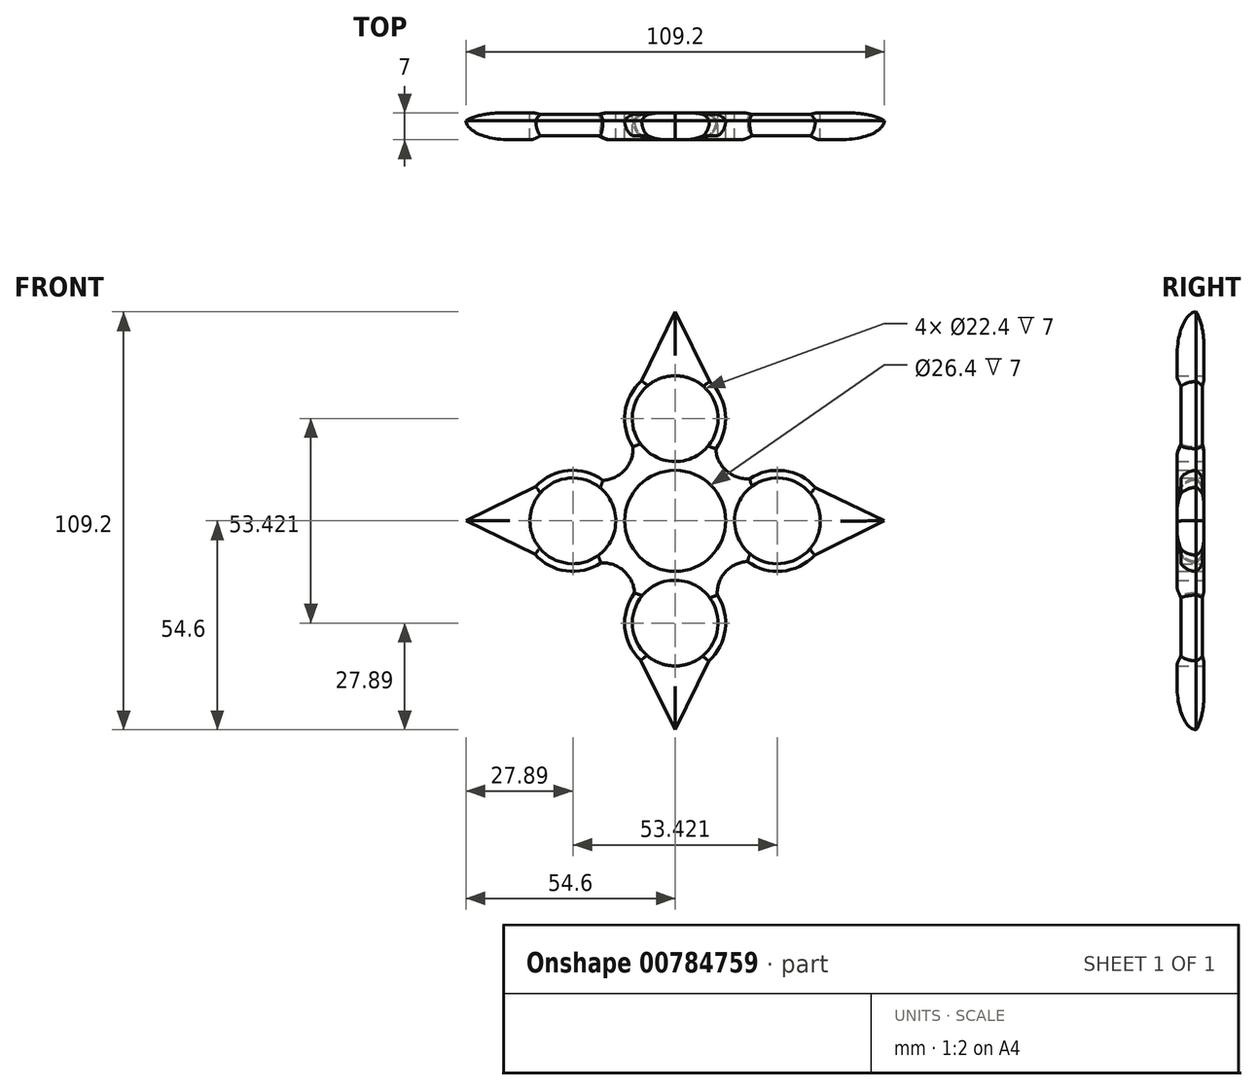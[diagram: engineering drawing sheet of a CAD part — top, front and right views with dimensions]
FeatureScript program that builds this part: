
annotation { "Feature Type Name" : "Feature", "Feature Type Description" : "" }
export const myFeature = defineFeature(function(context is Context, id is Id, definition is map)
    precondition{}
    {
        {
            var Q0;
            Q0=qCreatedBy(makeId("Front.planeOp"),FACE);
            var sketch = newSketch(context, id + "F0", { "sketchPlane" : qUnion([Q0])});
            skCircle(sketch, "E0", {"center": v(0, 0) * mm, "radius": 11.2 * mm});
            skCircle(sketch, "E1", {"center": v(0, 0) * mm, "radius": 13.2 * mm});
            skCircle(sketch, "E2", {"center": v(0, 26.71) * mm, "radius": 11.2 * mm});
            skArc(sketch, "E3", {"start": v(10.62, 18.87) * mm, "mid": v(0.33, 39.9) * mm, "end": v(-11, 19.4) * mm});
            skArc(sketch, "E4.1.0", {"start": v(-18.87, 10.62) * mm, "mid": v(-39.9, 0.33) * mm, "end": v(-19.4, -11) * mm});
            skCircle(sketch, "E4.1.1", {"center": v(-26.71, 0) * mm, "radius": 11.2 * mm});
            skArc(sketch, "E4.2.0", {"start": v(-10.62, -18.87) * mm, "mid": v(-0.33, -39.9) * mm, "end": v(11, -19.4) * mm});
            skCircle(sketch, "E4.2.1", {"center": v(0, -26.71) * mm, "radius": 11.2 * mm});
            skArc(sketch, "E5.1.3.0", {"start": v(18.87, -10.62) * mm, "mid": v(39.9, -0.33) * mm, "end": v(19.4, 11) * mm});
            skCircle(sketch, "E5.2.3.0", {"center": v(26.71, 0) * mm, "radius": 11.2 * mm});
            skArc(sketch, "E6", {"start": v(-18.87, 10.62) * mm, "mid": v(-13.1, 13.37) * mm, "end": v(-11, 19.4) * mm});
            skArc(sketch, "E7.1.0", {"start": v(-10.62, -18.87) * mm, "mid": v(-13.37, -13.1) * mm, "end": v(-19.4, -11) * mm});
            skArc(sketch, "E7.2.0", {"start": v(18.87, -10.62) * mm, "mid": v(13.1, -13.37) * mm, "end": v(11, -19.4) * mm});
            skArc(sketch, "E7.3.0", {"start": v(10.62, 18.87) * mm, "mid": v(13.37, 13.1) * mm, "end": v(19.4, 11) * mm});
            skLineSegment(sketch, "E8", {"start": v(-8.75, 36.6) * mm, "end": v(0, 54.6) * mm});
            skLineSegment(sketch, "E9", {"start": v(0, 54.6) * mm, "end": v(8.96, 36.4) * mm});
            skLineSegment(sketch, "E10.1.0", {"start": v(-54.6, 0) * mm, "end": v(-36.4, 8.96) * mm});
            skLineSegment(sketch, "E10.1.1", {"start": v(-36.6, -8.75) * mm, "end": v(-54.6, 0) * mm});
            skLineSegment(sketch, "E10.2.0", {"start": v(0, -54.6) * mm, "end": v(-8.96, -36.4) * mm});
            skLineSegment(sketch, "E10.2.1", {"start": v(8.75, -36.6) * mm, "end": v(0, -54.6) * mm});
            skLineSegment(sketch, "E10.3.0", {"start": v(54.6, 0) * mm, "end": v(36.4, -8.96) * mm});
            skLineSegment(sketch, "E10.3.1", {"start": v(36.6, 8.75) * mm, "end": v(54.6, 0) * mm});
            skSolve(sketch);
        }
        {
            var Q0;
            Q0=makeQuery(id+"F0.imprint","IMPRINT",FACE,{"disambiguationData":[TD([[makeQuery(id+"F0.imprint","IMPRINT",EDGE,{"derivedFrom":sQuery(id+"F0.wireOp",EDGE,"E1")}),-1.0]])]});
            var Q1;
            {var subQ0=sQuery(id+"F0.wireOp",EDGE,"E8");Q1=makeQuery(id+"F0.imprint","IMPRINT",FACE,{"disambiguationData":[TD([[makeQuery(id+"F0.imprint","IMPRINT",EDGE,{"derivedFrom":subQ0}),-1.0]])]});}
            var Q2;
            {var subQ0=sQuery(id+"F0.wireOp",EDGE,"E10.1.0");Q2=makeQuery(id+"F0.imprint","IMPRINT",FACE,{"disambiguationData":[TD([[makeQuery(id+"F0.imprint","IMPRINT",EDGE,{"derivedFrom":subQ0}),-1.0]])]});}
            var Q3;
            {var subQ0=sQuery(id+"F0.wireOp",EDGE,"E10.3.0");Q3=makeQuery(id+"F0.imprint","IMPRINT",FACE,{"disambiguationData":[TD([[makeQuery(id+"F0.imprint","IMPRINT",EDGE,{"derivedFrom":subQ0}),-1.0]])]});}
            var Q4;
            {var subQ0=sQuery(id+"F0.wireOp",EDGE,"E10.2.0");Q4=makeQuery(id+"F0.imprint","IMPRINT",FACE,{"disambiguationData":[TD([[makeQuery(id+"F0.imprint","IMPRINT",EDGE,{"derivedFrom":subQ0}),-1.0]])]});}
            extrude(context, id + "F1", {"entities" : qUnion([Q0, Q1, Q2, Q3, Q4]), "depth" : 7 * mm, "offsetDistance" : 25 * mm});
        }
        {
            var Q0;
            {var subQ0=sQuery(id+"F0.wireOp",EDGE,"E3");Q0=makeQuery(id+"F1.opExtrude","CAP_EDGE",EDGE,{"disambiguationData":[OSD([subQ0]),TDD([makeQuery(id+"F0.imprint","IMPRINT",EDGE,{"disambiguationData":[TD([[makeQuery(id+"F0.imprint","INTERSECT",VERTEX,{"derivedFrom":[subQ0,sQuery(id+"F0.wireOp",EDGE,"E6")]}),1.0]])],"derivedFrom":subQ0})])],"isStart":false});}
            var Q1;
            Q1=makeQuery(id+"F1.opExtrude","CAP_EDGE",EDGE,{"disambiguationData":[OSD([sQuery(id+"F0.wireOp",EDGE,"E8")])],"isStart":false});
            var Q2;
            Q2=makeQuery(id+"F1.opExtrude","CAP_EDGE",EDGE,{"disambiguationData":[OSD([sQuery(id+"F0.wireOp",EDGE,"E9")])],"isStart":false});
            var Q3;
            {var subQ0=sQuery(id+"F0.wireOp",EDGE,"E3");Q3=makeQuery(id+"F1.opExtrude","CAP_EDGE",EDGE,{"disambiguationData":[OSD([subQ0]),TDD([makeQuery(id+"F0.imprint","IMPRINT",EDGE,{"disambiguationData":[TD([[makeQuery(id+"F0.imprint","INTERSECT",VERTEX,{"derivedFrom":[subQ0,sQuery(id+"F0.wireOp",EDGE,"E7.3.0")]}),-1.0]])],"derivedFrom":subQ0})])],"isStart":false});}
            var Q4;
            Q4=makeQuery(id+"F1.opExtrude","CAP_EDGE",EDGE,{"disambiguationData":[OSD([sQuery(id+"F0.wireOp",EDGE,"E7.3.0")])],"isStart":false});
            var Q5;
            {var subQ0=sQuery(id+"F0.wireOp",EDGE,"E5.1.3.0");Q5=makeQuery(id+"F1.opExtrude","CAP_EDGE",EDGE,{"disambiguationData":[OSD([subQ0]),TDD([makeQuery(id+"F0.imprint","IMPRINT",EDGE,{"disambiguationData":[TD([[makeQuery(id+"F0.imprint","INTERSECT",VERTEX,{"derivedFrom":[subQ0,sQuery(id+"F0.wireOp",EDGE,"E7.3.0")]}),1.0]])],"derivedFrom":subQ0})])],"isStart":false});}
            var Q6;
            Q6=makeQuery(id+"F1.opExtrude","CAP_EDGE",EDGE,{"disambiguationData":[OSD([sQuery(id+"F0.wireOp",EDGE,"E10.3.1")])],"isStart":false});
            var Q7;
            Q7=makeQuery(id+"F1.opExtrude","CAP_EDGE",EDGE,{"disambiguationData":[OSD([sQuery(id+"F0.wireOp",EDGE,"E10.3.0")])],"isStart":false});
            var Q8;
            {var subQ0=sQuery(id+"F0.wireOp",EDGE,"E5.1.3.0");Q8=makeQuery(id+"F1.opExtrude","CAP_EDGE",EDGE,{"disambiguationData":[OSD([subQ0]),TDD([makeQuery(id+"F0.imprint","IMPRINT",EDGE,{"disambiguationData":[TD([[makeQuery(id+"F0.imprint","INTERSECT",VERTEX,{"derivedFrom":[subQ0,sQuery(id+"F0.wireOp",EDGE,"E7.2.0")]}),-1.0]])],"derivedFrom":subQ0})])],"isStart":false});}
            var Q9;
            Q9=makeQuery(id+"F1.opExtrude","CAP_EDGE",EDGE,{"disambiguationData":[OSD([sQuery(id+"F0.wireOp",EDGE,"E7.2.0")])],"isStart":false});
            var Q10;
            {var subQ0=sQuery(id+"F0.wireOp",EDGE,"E4.2.0");Q10=makeQuery(id+"F1.opExtrude","CAP_EDGE",EDGE,{"disambiguationData":[OSD([subQ0]),TDD([makeQuery(id+"F0.imprint","IMPRINT",EDGE,{"disambiguationData":[TD([[makeQuery(id+"F0.imprint","INTERSECT",VERTEX,{"derivedFrom":[subQ0,sQuery(id+"F0.wireOp",EDGE,"E7.2.0")]}),1.0]])],"derivedFrom":subQ0})])],"isStart":false});}
            var Q11;
            Q11=makeQuery(id+"F1.opExtrude","CAP_EDGE",EDGE,{"disambiguationData":[OSD([sQuery(id+"F0.wireOp",EDGE,"E10.2.1")])],"isStart":false});
            var Q12;
            Q12=makeQuery(id+"F1.opExtrude","CAP_EDGE",EDGE,{"disambiguationData":[OSD([sQuery(id+"F0.wireOp",EDGE,"E10.2.0")])],"isStart":false});
            var Q13;
            {var subQ0=sQuery(id+"F0.wireOp",EDGE,"E4.2.0");Q13=makeQuery(id+"F1.opExtrude","CAP_EDGE",EDGE,{"disambiguationData":[OSD([subQ0]),TDD([makeQuery(id+"F0.imprint","IMPRINT",EDGE,{"disambiguationData":[TD([[makeQuery(id+"F0.imprint","INTERSECT",VERTEX,{"derivedFrom":[subQ0,sQuery(id+"F0.wireOp",EDGE,"E7.1.0")]}),-1.0]])],"derivedFrom":subQ0})])],"isStart":false});}
            var Q14;
            Q14=makeQuery(id+"F1.opExtrude","CAP_EDGE",EDGE,{"disambiguationData":[OSD([sQuery(id+"F0.wireOp",EDGE,"E7.1.0")])],"isStart":false});
            var Q15;
            {var subQ0=sQuery(id+"F0.wireOp",EDGE,"E4.1.0");Q15=makeQuery(id+"F1.opExtrude","CAP_EDGE",EDGE,{"disambiguationData":[OSD([subQ0]),TDD([makeQuery(id+"F0.imprint","IMPRINT",EDGE,{"disambiguationData":[TD([[makeQuery(id+"F0.imprint","INTERSECT",VERTEX,{"derivedFrom":[subQ0,sQuery(id+"F0.wireOp",EDGE,"E7.1.0")]}),1.0]])],"derivedFrom":subQ0})])],"isStart":false});}
            var Q16;
            Q16=makeQuery(id+"F1.opExtrude","CAP_EDGE",EDGE,{"disambiguationData":[OSD([sQuery(id+"F0.wireOp",EDGE,"E10.1.1")])],"isStart":false});
            var Q17;
            Q17=makeQuery(id+"F1.opExtrude","CAP_EDGE",EDGE,{"disambiguationData":[OSD([sQuery(id+"F0.wireOp",EDGE,"E10.1.0")])],"isStart":false});
            var Q18;
            {var subQ0=sQuery(id+"F0.wireOp",EDGE,"E4.1.0");Q18=makeQuery(id+"F1.opExtrude","CAP_EDGE",EDGE,{"disambiguationData":[OSD([subQ0]),TDD([makeQuery(id+"F0.imprint","IMPRINT",EDGE,{"disambiguationData":[TD([[makeQuery(id+"F0.imprint","INTERSECT",VERTEX,{"derivedFrom":[subQ0,sQuery(id+"F0.wireOp",EDGE,"E6")]}),-1.0]])],"derivedFrom":subQ0})])],"isStart":false});}
            var Q19;
            Q19=makeQuery(id+"F1.opExtrude","CAP_EDGE",EDGE,{"disambiguationData":[OSD([sQuery(id+"F0.wireOp",EDGE,"E6")])],"isStart":false});
            fillet(context, id + "F2", {"entities" : qUnion([Q0, Q1, Q2, Q3, Q4, Q5, Q6, Q7, Q8, Q9, Q10, Q11, Q12, Q13, Q14, Q15, Q16, Q17, Q18, Q19]), "radius" : 5 * mm, "tangentPropagation" : true, "allowEdgeOverflow" : false});
        }
        {
            var Q0;
            Q0=makeQuery(id+"F1.opExtrude","CAP_EDGE",EDGE,{"disambiguationData":[OSD([sQuery(id+"F0.wireOp",EDGE,"E9")])],"isStart":true});
            var Q1;
            Q1=makeQuery(id+"F1.opExtrude","CAP_EDGE",EDGE,{"disambiguationData":[OSD([sQuery(id+"F0.wireOp",EDGE,"E8")])],"isStart":true});
            var Q2;
            Q2=makeQuery(id+"F1.opExtrude","CAP_EDGE",EDGE,{"disambiguationData":[OSD([sQuery(id+"F0.wireOp",EDGE,"E7.3.0")])],"isStart":true});
            var Q3;
            Q3=makeQuery(id+"F1.opExtrude","CAP_EDGE",EDGE,{"disambiguationData":[OSD([sQuery(id+"F0.wireOp",EDGE,"E6")])],"isStart":true});
            var Q4;
            Q4=makeQuery(id+"F1.opExtrude","CAP_EDGE",EDGE,{"disambiguationData":[OSD([sQuery(id+"F0.wireOp",EDGE,"E7.2.0")])],"isStart":true});
            var Q5;
            Q5=makeQuery(id+"F1.opExtrude","CAP_EDGE",EDGE,{"disambiguationData":[OSD([sQuery(id+"F0.wireOp",EDGE,"E7.1.0")])],"isStart":true});
            var Q6;
            Q6=makeQuery(id+"F1.opExtrude","CAP_EDGE",EDGE,{"disambiguationData":[OSD([sQuery(id+"F0.wireOp",EDGE,"E10.3.1")])],"isStart":true});
            var Q7;
            Q7=makeQuery(id+"F1.opExtrude","CAP_EDGE",EDGE,{"disambiguationData":[OSD([sQuery(id+"F0.wireOp",EDGE,"E10.3.0")])],"isStart":true});
            var Q8;
            Q8=makeQuery(id+"F1.opExtrude","CAP_EDGE",EDGE,{"disambiguationData":[OSD([sQuery(id+"F0.wireOp",EDGE,"E10.1.1")])],"isStart":true});
            var Q9;
            Q9=makeQuery(id+"F1.opExtrude","CAP_EDGE",EDGE,{"disambiguationData":[OSD([sQuery(id+"F0.wireOp",EDGE,"E10.1.0")])],"isStart":true});
            var Q10;
            Q10=makeQuery(id+"F1.opExtrude","CAP_EDGE",EDGE,{"disambiguationData":[OSD([sQuery(id+"F0.wireOp",EDGE,"E10.2.0")])],"isStart":true});
            var Q11;
            Q11=makeQuery(id+"F1.opExtrude","CAP_EDGE",EDGE,{"disambiguationData":[OSD([sQuery(id+"F0.wireOp",EDGE,"E10.2.1")])],"isStart":true});
            fillet(context, id + "F3", {"entities" : qUnion([Q0, Q1, Q2, Q3, Q4, Q5, Q6, Q7, Q8, Q9, Q10, Q11]), "radius" : 5 * mm, "tangentPropagation" : true, "allowEdgeOverflow" : false});
        }
        {
            var Q0;
            {var subQ0=sQuery(id+"F0.wireOp",EDGE,"E5.1.3.0");Q0=makeQuery(id+"F1.opExtrude","CAP_EDGE",EDGE,{"disambiguationData":[OSD([subQ0]),TDD([makeQuery(id+"F0.imprint","IMPRINT",EDGE,{"disambiguationData":[TD([[makeQuery(id+"F0.imprint","INTERSECT",VERTEX,{"derivedFrom":[subQ0,sQuery(id+"F0.wireOp",EDGE,"E7.3.0")]}),1.0]])],"derivedFrom":subQ0})])],"isStart":true});}
            var Q1;
            {var subQ0=sQuery(id+"F0.wireOp",EDGE,"E5.1.3.0");Q1=makeQuery(id+"F1.opExtrude","CAP_EDGE",EDGE,{"disambiguationData":[OSD([subQ0]),TDD([makeQuery(id+"F0.imprint","IMPRINT",EDGE,{"disambiguationData":[TD([[makeQuery(id+"F0.imprint","INTERSECT",VERTEX,{"derivedFrom":[subQ0,sQuery(id+"F0.wireOp",EDGE,"E7.2.0")]}),-1.0]])],"derivedFrom":subQ0})])],"isStart":true});}
            var Q2;
            {var subQ0=sQuery(id+"F0.wireOp",EDGE,"E4.2.0");Q2=makeQuery(id+"F1.opExtrude","CAP_EDGE",EDGE,{"disambiguationData":[OSD([subQ0]),TDD([makeQuery(id+"F0.imprint","IMPRINT",EDGE,{"disambiguationData":[TD([[makeQuery(id+"F0.imprint","INTERSECT",VERTEX,{"derivedFrom":[subQ0,sQuery(id+"F0.wireOp",EDGE,"E7.2.0")]}),1.0]])],"derivedFrom":subQ0})])],"isStart":true});}
            var Q3;
            {var subQ0=sQuery(id+"F0.wireOp",EDGE,"E4.2.0");Q3=makeQuery(id+"F1.opExtrude","CAP_EDGE",EDGE,{"disambiguationData":[OSD([subQ0]),TDD([makeQuery(id+"F0.imprint","IMPRINT",EDGE,{"disambiguationData":[TD([[makeQuery(id+"F0.imprint","INTERSECT",VERTEX,{"derivedFrom":[subQ0,sQuery(id+"F0.wireOp",EDGE,"E7.1.0")]}),-1.0]])],"derivedFrom":subQ0})])],"isStart":true});}
            var Q4;
            {var subQ0=sQuery(id+"F0.wireOp",EDGE,"E4.1.0");Q4=makeQuery(id+"F1.opExtrude","CAP_EDGE",EDGE,{"disambiguationData":[OSD([subQ0]),TDD([makeQuery(id+"F0.imprint","IMPRINT",EDGE,{"disambiguationData":[TD([[makeQuery(id+"F0.imprint","INTERSECT",VERTEX,{"derivedFrom":[subQ0,sQuery(id+"F0.wireOp",EDGE,"E7.1.0")]}),1.0]])],"derivedFrom":subQ0})])],"isStart":true});}
            var Q5;
            {var subQ0=sQuery(id+"F0.wireOp",EDGE,"E4.1.0");Q5=makeQuery(id+"F1.opExtrude","CAP_EDGE",EDGE,{"disambiguationData":[OSD([subQ0]),TDD([makeQuery(id+"F0.imprint","IMPRINT",EDGE,{"disambiguationData":[TD([[makeQuery(id+"F0.imprint","INTERSECT",VERTEX,{"derivedFrom":[subQ0,sQuery(id+"F0.wireOp",EDGE,"E6")]}),-1.0]])],"derivedFrom":subQ0})])],"isStart":true});}
            var Q6;
            {var subQ0=sQuery(id+"F0.wireOp",EDGE,"E3");Q6=makeQuery(id+"F1.opExtrude","CAP_EDGE",EDGE,{"disambiguationData":[OSD([subQ0]),TDD([makeQuery(id+"F0.imprint","IMPRINT",EDGE,{"disambiguationData":[TD([[makeQuery(id+"F0.imprint","INTERSECT",VERTEX,{"derivedFrom":[subQ0,sQuery(id+"F0.wireOp",EDGE,"E6")]}),1.0]])],"derivedFrom":subQ0})])],"isStart":true});}
            var Q7;
            {var subQ0=sQuery(id+"F0.wireOp",EDGE,"E3");Q7=makeQuery(id+"F1.opExtrude","CAP_EDGE",EDGE,{"disambiguationData":[OSD([subQ0]),TDD([makeQuery(id+"F0.imprint","IMPRINT",EDGE,{"disambiguationData":[TD([[makeQuery(id+"F0.imprint","INTERSECT",VERTEX,{"derivedFrom":[subQ0,sQuery(id+"F0.wireOp",EDGE,"E7.3.0")]}),-1.0]])],"derivedFrom":subQ0})])],"isStart":true});}
            fillet(context, id + "F4", {"entities" : qUnion([Q0, Q1, Q2, Q3, Q4, Q5, Q6, Q7]), "radius" : 5 * mm, "tangentPropagation" : true, "allowEdgeOverflow" : false});
        }
    });
